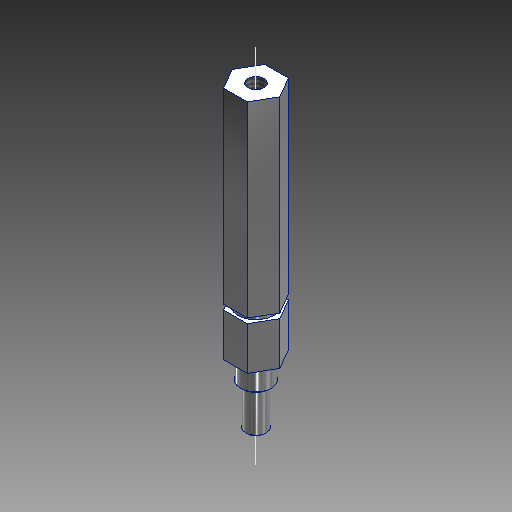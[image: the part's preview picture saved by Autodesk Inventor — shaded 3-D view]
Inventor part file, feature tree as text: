
AUTODESK INVENTOR PART (.ipt)
format: ipt  version: 2018 (Build 220112000, 112)  size: 168,960 bytes
history: native  units: in
note: dims shown in document units (in); Inventor stores cm internally (conversion verified against a paired STEP export)
features: other x3, delete_face x1, hole x1, extrude x1, imported_body x1, sketch x1, projected_geometry x1
ambient origin geometry x8: Origin, YZ Plane, XZ Plane, XY Plane, X Axis, Y Axis, Z Axis, Center Point
bodies: Body1 (feature_tree)
feature tree (9):
  other  "Toughbox_d03"
  other  "Toughbox_d03.ipt1"
  other  "Work Axis1"
  delete_face  "Delete Face1"
  hole  "Hole1"  [1 undecoded]
  extrude  "Extrusion1"  [1 undecoded]
  imported_body  "Base1"
  sketch  "Sketch1"  dims[d15=0.3937in d16=0.3937in d6=0.196in d7=0.5in d8=0.1575in d9=0.0787in d10=90.0deg d11=0.625in d12=0.8108in d13=0.3937in d14=0.0in]
  projected_geometry  "Projected Loop1"
note: 2 required parameter values undecoded (feature->parameter linkage not recoverable at this tier; creation-order binding heuristic only, values carry confidence <= 0.55)
